FREECAD ASSEMBLY — COMPONENT RECIPES ("InterconnectIO_Box_full_511-1000")

This assembly document has 5 components, labeled P0..P4 below (a component is one placed body or linked part). 2 of them carry a construction recipe — the FreeCAD feature program that regenerates the part from scratch, quoted from this document or its linked companion documents; the rest are supplied as boundary geometry only. No exploded tour is included for this assembly.
COMPONENT P0 — recipe-attached ("rail_left", modeled in this document).
Construction recipe (the document's own serialized feature program — sketch geometry with constraints, then the solid features built on it; lengths are millimeters unless a unit is written):

FEATURE [PartDesign::Body] Body  label="slot"
  Origin = -> Origin119
  Placement = pos=(0,6.008,0) rot=(0,0,1;0rad)
FEATURE [Sketcher::SketchObject] Sketch
  FullyConstrained = true
  MapMode = 5
  Support = -> [XY_Plane120]
  sketch-geometry (4):
    g0: LineSegment StartX=-2.36 StartY=2.5 StartZ=0 EndX=2.36 EndY=2.5 EndZ=0
    g1: LineSegment StartX=2.36 StartY=2.5 StartZ=0 EndX=2.36 EndY=156 EndZ=0
    g2: LineSegment StartX=2.36 StartY=156 StartZ=0 EndX=-2.36 EndY=156 EndZ=0
    g3: LineSegment StartX=-2.36 StartY=156 StartZ=0 EndX=-2.36 EndY=2.5 EndZ=0
  constraints (12):
    c: Coincident(g0,g1)
    c: Coincident(g1,g2)
    c: Coincident(g2,g3)
    c: Coincident(g3,g0)
    c: Horizontal(g0)
    c: Horizontal(g2)
    c: Vertical(g1)
    c: Vertical(g3)
    c: DistanceX(g2,g2) = 4.72
    c: DistanceY(g0,g-1) = -2.5
    c: DistanceX(g0,g-1) = 2.36
    c: DistanceY(g1,g1) = 153.5
FEATURE [Sketcher::SketchObject] Sketch003
  FullyConstrained = true
  MapMode = 5
  Support = -> [XY_Plane120]
  sketch-geometry (8):
    g0: LineSegment StartX=-1 StartY=0 StartZ=0 EndX=-1 EndY=153 EndZ=0
    g1: ArcOfCircle CenterX=-7.01053 CenterY=152.083 CenterZ=0 NormalX=0 NormalY=0 NormalZ=1 AngleXU=0 Radius=6.08 StartAngle=0.151318 EndAngle=0.699927
    g2: LineSegment StartX=-2.36 StartY=156 StartZ=0 EndX=-2.86 EndY=156 EndZ=0
    g3: ArcOfCircle CenterX=-3459.01 CenterY=157.297 CenterZ=0 NormalX=0 NormalY=0 NormalZ=1 AngleXU=0 Radius=3456.16 StartAngle=6.24055 EndAngle=6.28281
    g4: LineSegment StartX=-4 StartY=0 StartZ=0 EndX=-4 EndY=2.5 EndZ=0
    g5: LineSegment StartX=-4 StartY=2.5 StartZ=0 EndX=-6 EndY=2.5 EndZ=0
    g6: LineSegment StartX=-4 StartY=0 StartZ=0 EndX=-1 EndY=0 EndZ=0
    g7: LineSegment StartX=-6 StartY=10 StartZ=0 EndX=-6 EndY=2.5 EndZ=0
  constraints (27):
    c: Vertical(g0)
    c: Coincident(g1,g0)
    c: Coincident(g2,g1)
    c: Horizontal(g2)
    c: Coincident(g3,g2)
    c: DistanceX(g2,g2) = 0.5
    c: Diameter(g3) = 6912.31
    c: PointOnObject(g6,g-1)
    c: Vertical(g4)
    c: Coincident(g5,g4)
    c: Horizontal(g5)
    c: Coincident(g6,g4)
    c: Coincident(g7,g3)
    c: Coincident(g7,g5)
    c: DistanceX(g6,g6) = 3
    c: Vertical(g7)
    c: DistanceX(g5,g5) = 2
    c: DistanceY(g7,g7) = 7.5
    c: DistanceY(g4,g4) = 2.5
    c: DistanceY(g4,g-1) = 0
    c: DistanceY(g3,g2) = 146
    c: DistanceY(g0,g0) = 153
    c: DistanceX(g0,g-1) = 1
    c: DistanceX(g6,g-1) = 1
    c: DistanceY(g6,g0) = 0
    c: Radius(g1) = 6.08
    c: DistanceX(g1,g0) = 1.36
FEATURE [PartDesign::Pad] Pad
  Direction = (0,0,1)
  Length = 8
  Length2 = 10
  Profile = -> Sketch003
  ReferenceAxis = -> Sketch003 [N_Axis]
  Type = 0
FEATURE [PartDesign::Pad] Pad001
  BaseFeature = -> Pad
  Direction = (0,0,1)
  Length = 5
  Length2 = 10
  Profile = -> Sketch
  ReferenceAxis = -> Sketch [N_Axis]
  Type = 0
FEATURE [Sketcher::SketchObject] Sketch011
  FullyConstrained = true
  MapMode = 5
  Support = -> [XY_Plane120]
  sketch-geometry (6):
    g0: LineSegment StartX=1 StartY=0 StartZ=0 EndX=10 EndY=0 EndZ=0
    g1: LineSegment StartX=4.36 StartY=156 StartZ=0 EndX=2.36 EndY=156 EndZ=0
    g2: LineSegment StartX=1 StartY=153 StartZ=0 EndX=1 EndY=0 EndZ=0
    g3: ArcOfCircle CenterX=7.01053 CenterY=152.083 CenterZ=0 NormalX=0 NormalY=0 NormalZ=1 AngleXU=0 Radius=6.08 StartAngle=2.44167 EndAngle=2.99027
    g4: LineSegment StartX=10 StartY=0 StartZ=0 EndX=10 EndY=10.5 EndZ=0
    g5: ArcOfCircle CenterX=-6386.74 CenterY=-164.597 CenterZ=0 NormalX=0 NormalY=0 NormalZ=1 AngleXU=0 Radius=6399.14 StartAngle=0.027366 EndAngle=0.050121
  constraints (20):
    c: Coincident(g2,g0)
    c: Horizontal(g0)
    c: Horizontal(g1)
    c: Vertical(g2)
    c: PointOnObject(g0,g-1)
    c: Coincident(g1,g3)
    c: Coincident(g2,g3)
    c: DistanceX(g2,g1) = 1.36
    c: DistanceY(g2,g1) = 3
    c: DistanceX(g1,g1) = 2
    c: DistanceX(g-1,g0) = 1
    c: DistanceY(g2,g2) = 153
    c: Radius(g3) = 6.08
    c: Coincident(g4,g0)
    c: DistanceY(g4,g4) = 10.5
    c: Coincident(g5,g4)
    c: Coincident(g5,g1)
    c: Radius(g5) = 6399.14
    c: DistanceX(g0,g0) = 9
    c: DistanceX(g-1,g4) = 10
FEATURE [PartDesign::Pad] Pad003
  BaseFeature = -> Pad001
  Direction = (0,0,1)
  Length = 8
  Length2 = 10
  Profile = -> Sketch011
  ReferenceAxis = -> Sketch011 [N_Axis]
  Type = 0
FEATURE [PartDesign::Body] Body003  label="rail"
  Group = -> [Sketch003,Pad,Sketch,Pad001,Sketch011,Pad003]
  Origin = -> Origin120
  Tip = -> Pad003
FEATURE [Sketcher::SketchObject] Sketch013
  FullyConstrained = false
  MapMode = 5
  Placement = pos=(0,0,0) rot=(0.57735,0.57735,0.57735;2.0944rad)
  Support = -> [YZ_Plane121]
  sketch-geometry (5):
    g0: LineSegment StartX=6.01175 StartY=0 StartZ=0 EndX=36.0118 EndY=0 EndZ=0
    g1: LineSegment StartX=36.0118 StartY=0 StartZ=0 EndX=36.0118 EndY=-2 EndZ=0
    g2: LineSegment StartX=8.01175 StartY=-30 StartZ=0 EndX=6.01175 EndY=-30 EndZ=0
    g3: LineSegment StartX=6.01175 StartY=-30 StartZ=0 EndX=6.01175 EndY=0 EndZ=0
    g4: ArcOfCircle CenterX=42.4201 CenterY=-36.4083 CenterZ=0 NormalX=0 NormalY=0 NormalZ=1 AngleXU=0 Radius=35 StartAngle=1.75493 EndAngle=2.95746
  constraints (14):
    c: Coincident(g0,g1)
    c: Coincident(g2,g3)
    c: Coincident(g3,g0)
    c: Horizontal(g0)
    c: Horizontal(g2)
    c: Vertical(g1)
    c: Vertical(g3)
    c: PointOnObject(g0,g-1)
    c: DistanceX(g0,g0) = 30
    c: Coincident(g1,g4)
    c: Coincident(g2,g4)
    c: DistanceY(g1,g1) = 2
    c: DistanceX(g2,g2) = 2
    c: Radius(g4) = 35
FEATURE [PartDesign::Pad] Pad005
  Direction = (1,-2e-16,3e-16)
  Length = 6
  Length2 = 10
  Placement = pos=(0,0,0) rot=(0.57735,0.57735,0.57735;2.0944rad)
  Profile = -> Sketch013
  ReferenceAxis = -> Sketch013 [N_Axis]
  Type = 0
FEATURE [PartDesign::Fillet] Fillet
  Base = -> Pad005 [Edge5]
  BaseFeature = -> Pad005
  Placement = pos=(0,0,0) rot=(0.57735,0.57735,0.57735;2.0944rad)
  Radius = 2
  SupportTransform = false
  UseAllEdges = false
FEATURE [PartDesign::Fillet] Fillet001
  Base = -> Fillet [Edge17]
  BaseFeature = -> Fillet
  Placement = pos=(0,0,0) rot=(0.57735,0.57735,0.57735;2.0944rad)
  Radius = 2
  SupportTransform = false
  UseAllEdges = false
FEATURE [PartDesign::Body] Body004  label="sideforce"
  Group = -> [Sketch013,Pad005,Fillet,Fillet001]
  Origin = -> Origin121
  Placement = pos=(-4.016,0.057,0) rot=(0,0,1;0rad)
  Tip = -> Fillet001
FEATURE [Sketcher::SketchObject] Sketch019
  FullyConstrained = false
  MapMode = 5
  Placement = pos=(0,0,0) rot=(-0.57735,0.57735,0.57735;4.18879rad)
  Support = -> [YZ_Plane122]
  sketch-geometry (10):
    g0: LineSegment StartX=-156.003 StartY=8.00103 StartZ=0 EndX=-137.423 EndY=8.00103 EndZ=0
    g1: LineSegment StartX=-137.423 StartY=8.00103 StartZ=0 EndX=-137.423 EndY=8.88796 EndZ=0
    g2: LineSegment StartX=-139.803 StartY=35.8702 StartZ=0 EndX=-153.603 EndY=35.8702 EndZ=0
    g3: ArcOfCircle CenterX=-136.888 CenterY=21.0784 CenterZ=0 NormalX=0 NormalY=0 NormalZ=1 AngleXU=0 Radius=11.34 StartAngle=1.74764 EndAngle=4.59202
    g4: ArcOfCircle CenterX=-153.603 CenterY=33.4702 CenterZ=0 NormalX=0 NormalY=0 NormalZ=1 AngleXU=0 Radius=2.4 StartAngle=1.5708 EndAngle=3.27078
    g5: ArcOfCircle CenterX=-139.803 CenterY=33.4702 CenterZ=0 NormalX=0 NormalY=0 NormalZ=1 AngleXU=0 Radius=2.4 StartAngle=0.566257 EndAngle=1.5708
    g6: ArcOfCircle CenterX=-230.704 CenterY=20.6405 CenterZ=0 NormalX=0 NormalY=0 NormalZ=1 AngleXU=0 Radius=75.763 StartAngle=6.11557 EndAngle=6.44921
    g7: Circle CenterX=-150.473 CenterY=13.3301 CenterZ=0 NormalX=0 NormalY=0 NormalZ=1 AngleXU=0 Radius=3
    g8: ArcOfCircle CenterX=-138.362 CenterY=8.88796 CenterZ=0 NormalX=0 NormalY=0 NormalZ=1 AngleXU=0 Radius=0.939281 StartAngle=0 EndAngle=1.45042
    g9: ArcOfCircle CenterX=-139.174 CenterY=33.8702 CenterZ=0 NormalX=0 NormalY=0 NormalZ=1 AngleXU=0 Radius=1.65446 StartAngle=4.88923 EndAngle=6.84944
  constraints (20):
    c: Coincident(g0,g1)
    c: Horizontal(g0)
    c: Horizontal(g2)
    c: Vertical(g1)
    c: Tangent(g2,g4) = -1.5708
    c: Tangent(g2,g5) = -1.5708
    c: Radius(g4) = 2.4
    c: Radius(g5) = 2.4
    c: DistanceX(g2,g2) = 13.8
    c: DistanceY(g0,g4) = 25.16
    c: DistanceX(g4,g2) = 2.38
    c: Radius(g3) = 11.34
    c: Coincident(g6,g0)
    c: Coincident(g6,g4)
    c: DistanceX(g0,g0) = 18.58
    c: Diameter(g7) = 6
    c: Tangent(g3,g8) = 1.5708
    c: Tangent(g1,g8) = -1.5708
    c: Tangent(g3,g9) = 1.5708
    c: Tangent(g5,g9) = -1.5708
FEATURE [PartDesign::Pad] Pad006
  Direction = (-1,2e-16,-3e-16)
  Length = 7
  Length2 = 10
  Placement = pos=(0,0,0) rot=(0.57735,0.57735,0.57735;2.0944rad)
  Profile = -> Sketch019
  ReferenceAxis = -> Sketch019 [N_Axis]
  Type = 0
FEATURE [PartDesign::Body] Body007  label="finger"
  Group = -> [Sketch019,Pad006]
  Origin = -> Origin122
  Placement = pos=(-2.654,-0.011,8.013) rot=(0,1,0;3.14159rad)
  Tip = -> Pad006
FEATURE [Sketcher::SketchObject] Sketch020
  FullyConstrained = true
  MapMode = 5
  Placement = pos=(0,0,0) rot=(1,0,0;1.5708rad)
  Support = -> [XZ_Plane124]
  sketch-geometry (4):
    g0: ArcOfCircle CenterX=5.9 CenterY=35 CenterZ=0 NormalX=0 NormalY=0 NormalZ=1 AngleXU=0 Radius=3 StartAngle=4e-16 EndAngle=3.14159
    g1: ArcOfCircle CenterX=5.9 CenterY=13 CenterZ=0 NormalX=0 NormalY=0 NormalZ=1 AngleXU=0 Radius=3 StartAngle=3.14159 EndAngle=6.28319
    g2: LineSegment StartX=2.9 StartY=35 StartZ=0 EndX=2.9 EndY=13 EndZ=0
    g3: LineSegment StartX=8.9 StartY=13 StartZ=0 EndX=8.9 EndY=35 EndZ=0
  constraints (10):
    c: Tangent(g0,g2) = -1.5708
    c: Tangent(g2,g1) = -1.5708
    c: Tangent(g1,g3) = -1.5708
    c: Tangent(g3,g0) = -1.5708
    c: Equal(g0,g1)
    c: Vertical(g2)
    c: DistanceY(g1,g0) = 22
    c: DistanceX(g1,g1) = 6
    c: DistanceY(g-1,g1) = 13
    c: DistanceX(g-1,g1) = 5.9
FEATURE [PartDesign::Pad] Pad007
  Direction = (0,-1,-2e-16)
  Length = 2
  Length2 = 10
  Placement = pos=(0,0,0) rot=(1,0,0;1.5708rad)
  Profile = -> Sketch020
  ReferenceAxis = -> Sketch020 [N_Axis]
  Type = 0
FEATURE [PartDesign::Body] Body009  label="slotscrew"
  Group = -> [Sketch020,Pad007]
  Origin = -> Origin123
  Placement = pos=(-0.028,0.002,-39.747) rot=(0,0,1;0rad)
  Tip = -> Pad007
COMPONENT P1 — recipe-attached ("rail_right", modeled in this document).
Construction recipe (the document's own serialized feature program — sketch geometry with constraints, then the solid features built on it; lengths are millimeters unless a unit is written):

FEATURE [Sketcher::SketchObject] Sketch021
  AttachmentOffset = pos=(0,0,3) rot=(0,0,1;0rad)
  FullyConstrained = true
  MapMode = 5
  Placement = pos=(0,0,3) rot=(0,0,1;0rad)
  Support = -> [XY_Plane125]
  sketch-geometry (4):
    g0: LineSegment StartX=-2.36 StartY=2.5 StartZ=0 EndX=2.36 EndY=2.5 EndZ=0
    g1: LineSegment StartX=2.36 StartY=2.5 StartZ=0 EndX=2.36 EndY=156 EndZ=0
    g2: LineSegment StartX=2.36 StartY=156 StartZ=0 EndX=-2.36 EndY=156 EndZ=0
    g3: LineSegment StartX=-2.36 StartY=156 StartZ=0 EndX=-2.36 EndY=2.5 EndZ=0
  constraints (12):
    c: Coincident(g0,g1)
    c: Coincident(g1,g2)
    c: Coincident(g2,g3)
    c: Coincident(g3,g0)
    c: Horizontal(g0)
    c: Horizontal(g2)
    c: Vertical(g1)
    c: Vertical(g3)
    c: DistanceX(g2,g2) = 4.72
    c: DistanceY(g0,g-1) = -2.5
    c: DistanceX(g0,g-1) = 2.36
    c: DistanceY(g1,g1) = 153.5
FEATURE [Sketcher::SketchObject] Sketch022
  FullyConstrained = true
  MapMode = 5
  Support = -> [XY_Plane125]
  sketch-geometry (8):
    g0: LineSegment StartX=-1 StartY=0 StartZ=0 EndX=-1 EndY=153 EndZ=0
    g1: ArcOfCircle CenterX=-7.01053 CenterY=152.083 CenterZ=0 NormalX=0 NormalY=0 NormalZ=1 AngleXU=0 Radius=6.08 StartAngle=0.151318 EndAngle=0.699927
    g2: LineSegment StartX=-2.36 StartY=156 StartZ=0 EndX=-2.86 EndY=156 EndZ=0
    g3: ArcOfCircle CenterX=-3459.01 CenterY=157.297 CenterZ=0 NormalX=0 NormalY=0 NormalZ=1 AngleXU=0 Radius=3456.16 StartAngle=6.24055 EndAngle=6.28281
    g4: LineSegment StartX=-4 StartY=0 StartZ=0 EndX=-4 EndY=2.5 EndZ=0
    g5: LineSegment StartX=-4 StartY=2.5 StartZ=0 EndX=-6 EndY=2.5 EndZ=0
    g6: LineSegment StartX=-4 StartY=0 StartZ=0 EndX=-1 EndY=0 EndZ=0
    g7: LineSegment StartX=-6 StartY=10 StartZ=0 EndX=-6 EndY=2.5 EndZ=0
  constraints (27):
    c: Vertical(g0)
    c: Coincident(g1,g0)
    c: Coincident(g2,g1)
    c: Horizontal(g2)
    c: Coincident(g3,g2)
    c: DistanceX(g2,g2) = 0.5
    c: Diameter(g3) = 6912.31
    c: PointOnObject(g6,g-1)
    c: Vertical(g4)
    c: Coincident(g5,g4)
    c: Horizontal(g5)
    c: Coincident(g6,g4)
    c: Coincident(g7,g3)
    c: Coincident(g7,g5)
    c: DistanceX(g6,g6) = 3
    c: Vertical(g7)
    c: DistanceX(g5,g5) = 2
    c: DistanceY(g7,g7) = 7.5
    c: DistanceY(g4,g4) = 2.5
    c: DistanceY(g4,g-1) = 0
    c: DistanceY(g3,g2) = 146
    c: DistanceY(g0,g0) = 153
    c: DistanceX(g0,g-1) = 1
    c: DistanceX(g6,g-1) = 1
    c: DistanceY(g6,g0) = 0
    c: Radius(g1) = 6.08
    c: DistanceX(g1,g0) = 1.36
FEATURE [PartDesign::Pad] Pad008
  Direction = (0,0,1)
  Length = 8
  Length2 = 10
  Profile = -> Sketch022
  ReferenceAxis = -> Sketch022 [N_Axis]
  Type = 0
FEATURE [PartDesign::Pad] Pad009
  BaseFeature = -> Pad008
  Direction = (0,0,1)
  Length = 5
  Length2 = 10
  Profile = -> Sketch021
  ReferenceAxis = -> Sketch021 [N_Axis]
  Type = 0
FEATURE [Sketcher::SketchObject] Sketch023
  FullyConstrained = true
  MapMode = 5
  Support = -> [XY_Plane125]
  sketch-geometry (6):
    g0: LineSegment StartX=1 StartY=0 StartZ=0 EndX=10 EndY=0 EndZ=0
    g1: LineSegment StartX=4.36 StartY=156 StartZ=0 EndX=2.36 EndY=156 EndZ=0
    g2: LineSegment StartX=1 StartY=153 StartZ=0 EndX=1 EndY=0 EndZ=0
    g3: ArcOfCircle CenterX=7.01053 CenterY=152.083 CenterZ=0 NormalX=0 NormalY=0 NormalZ=1 AngleXU=0 Radius=6.08 StartAngle=2.44167 EndAngle=2.99027
    g4: LineSegment StartX=10 StartY=0 StartZ=0 EndX=10 EndY=10.5 EndZ=0
    g5: ArcOfCircle CenterX=-6386.74 CenterY=-164.597 CenterZ=0 NormalX=0 NormalY=0 NormalZ=1 AngleXU=0 Radius=6399.14 StartAngle=0.027366 EndAngle=0.050121
  constraints (20):
    c: Coincident(g2,g0)
    c: Horizontal(g0)
    c: Horizontal(g1)
    c: Vertical(g2)
    c: PointOnObject(g0,g-1)
    c: Coincident(g1,g3)
    c: Coincident(g2,g3)
    c: DistanceX(g2,g1) = 1.36
    c: DistanceY(g2,g1) = 3
    c: DistanceX(g1,g1) = 2
    c: DistanceX(g-1,g0) = 1
    c: DistanceY(g2,g2) = 153
    c: Radius(g3) = 6.08
    c: Coincident(g4,g0)
    c: DistanceY(g4,g4) = 10.5
    c: Coincident(g5,g4)
    c: Coincident(g5,g1)
    c: Radius(g5) = 6399.14
    c: DistanceX(g0,g0) = 9
    c: DistanceX(g-1,g4) = 10
FEATURE [PartDesign::Pad] Pad010
  BaseFeature = -> Pad009
  Direction = (0,0,1)
  Length = 8
  Length2 = 10
  Profile = -> Sketch023
  ReferenceAxis = -> Sketch023 [N_Axis]
  Type = 0
FEATURE [PartDesign::Body] Body010  label="rail001"
  Group = -> [Sketch022,Pad008,Sketch021,Pad009,Sketch023,Pad010]
  Origin = -> Origin125
  Tip = -> Pad010
FEATURE [Sketcher::SketchObject] Sketch025
  FullyConstrained = false
  MapMode = 5
  Placement = pos=(0,0,0) rot=(0.57735,0.57735,0.57735;2.0944rad)
  Support = -> [YZ_Plane126]
  sketch-geometry (5):
    g0: LineSegment StartX=6.01175 StartY=0 StartZ=0 EndX=36.0118 EndY=0 EndZ=0
    g1: LineSegment StartX=36.0118 StartY=0 StartZ=0 EndX=36.0118 EndY=-2 EndZ=0
    g2: LineSegment StartX=8.01175 StartY=-30 StartZ=0 EndX=6.01175 EndY=-30 EndZ=0
    g3: LineSegment StartX=6.01175 StartY=-30 StartZ=0 EndX=6.01175 EndY=0 EndZ=0
    g4: ArcOfCircle CenterX=42.4201 CenterY=-36.4083 CenterZ=0 NormalX=0 NormalY=0 NormalZ=1 AngleXU=0 Radius=35 StartAngle=1.75493 EndAngle=2.95746
  constraints (14):
    c: Coincident(g0,g1)
    c: Coincident(g2,g3)
    c: Coincident(g3,g0)
    c: Horizontal(g0)
    c: Horizontal(g2)
    c: Vertical(g1)
    c: Vertical(g3)
    c: PointOnObject(g0,g-1)
    c: DistanceX(g0,g0) = 30
    c: Coincident(g1,g4)
    c: Coincident(g2,g4)
    c: DistanceY(g1,g1) = 2
    c: DistanceX(g2,g2) = 2
    c: Radius(g4) = 35
FEATURE [PartDesign::Pad] Pad012
  Direction = (1,-2e-16,3e-16)
  Length = 6
  Length2 = 10
  Placement = pos=(0,0,0) rot=(0.57735,0.57735,0.57735;2.0944rad)
  Profile = -> Sketch025
  ReferenceAxis = -> Sketch025 [N_Axis]
  Type = 0
FEATURE [PartDesign::Fillet] Fillet002
  Base = -> Pad012 [Edge5]
  BaseFeature = -> Pad012
  Placement = pos=(0,0,0) rot=(0.57735,0.57735,0.57735;2.0944rad)
  Radius = 2
  SupportTransform = false
  UseAllEdges = false
FEATURE [PartDesign::Fillet] Fillet003
  Base = -> Fillet002 [Edge17]
  BaseFeature = -> Fillet002
  Placement = pos=(0,0,0) rot=(0.57735,0.57735,0.57735;2.0944rad)
  Radius = 2
  SupportTransform = false
  UseAllEdges = false
FEATURE [PartDesign::Body] Body011  label="sideforce001"
  Group = -> [Sketch025,Pad012,Fillet002,Fillet003]
  Origin = -> Origin126
  Placement = pos=(2,0,8) rot=(0,1,0;3.14159rad)
  Tip = -> Fillet003
FEATURE [Sketcher::SketchObject] Sketch026
  FullyConstrained = false
  MapMode = 5
  Placement = pos=(0,0,0) rot=(-0.57735,0.57735,0.57735;4.18879rad)
  Support = -> [YZ_Plane127]
  sketch-geometry (10):
    g0: LineSegment StartX=-156.003 StartY=8.00103 StartZ=0 EndX=-137.423 EndY=8.00103 EndZ=0
    g1: LineSegment StartX=-137.423 StartY=8.00103 StartZ=0 EndX=-137.423 EndY=8.88796 EndZ=0
    g2: LineSegment StartX=-139.803 StartY=35.8702 StartZ=0 EndX=-153.603 EndY=35.8702 EndZ=0
    g3: ArcOfCircle CenterX=-136.888 CenterY=21.0784 CenterZ=0 NormalX=0 NormalY=0 NormalZ=1 AngleXU=0 Radius=11.34 StartAngle=1.74764 EndAngle=4.59202
    g4: ArcOfCircle CenterX=-153.603 CenterY=33.4702 CenterZ=0 NormalX=0 NormalY=0 NormalZ=1 AngleXU=0 Radius=2.4 StartAngle=1.5708 EndAngle=3.27078
    g5: ArcOfCircle CenterX=-139.803 CenterY=33.4702 CenterZ=0 NormalX=0 NormalY=0 NormalZ=1 AngleXU=0 Radius=2.4 StartAngle=0.566257 EndAngle=1.5708
    g6: ArcOfCircle CenterX=-230.704 CenterY=20.6405 CenterZ=0 NormalX=0 NormalY=0 NormalZ=1 AngleXU=0 Radius=75.763 StartAngle=6.11557 EndAngle=6.44921
    g7: Circle CenterX=-150.473 CenterY=13.3301 CenterZ=0 NormalX=0 NormalY=0 NormalZ=1 AngleXU=0 Radius=3
    g8: ArcOfCircle CenterX=-138.362 CenterY=8.88796 CenterZ=0 NormalX=0 NormalY=0 NormalZ=1 AngleXU=0 Radius=0.939281 StartAngle=0 EndAngle=1.45042
    g9: ArcOfCircle CenterX=-139.174 CenterY=33.8702 CenterZ=0 NormalX=0 NormalY=0 NormalZ=1 AngleXU=0 Radius=1.65446 StartAngle=4.88923 EndAngle=6.84944
  constraints (20):
    c: Coincident(g0,g1)
    c: Horizontal(g0)
    c: Horizontal(g2)
    c: Vertical(g1)
    c: Tangent(g2,g4) = -1.5708
    c: Tangent(g2,g5) = -1.5708
    c: Radius(g4) = 2.4
    c: Radius(g5) = 2.4
    c: DistanceX(g2,g2) = 13.8
    c: DistanceY(g0,g4) = 25.16
    c: DistanceX(g4,g2) = 2.38
    c: Radius(g3) = 11.34
    c: Coincident(g6,g0)
    c: Coincident(g6,g4)
    c: DistanceX(g0,g0) = 18.58
    c: Diameter(g7) = 6
    c: Tangent(g3,g8) = 1.5708
    c: Tangent(g1,g8) = -1.5708
    c: Tangent(g3,g9) = 1.5708
    c: Tangent(g5,g9) = -1.5708
FEATURE [PartDesign::Pad] Pad013
  Direction = (-1,2e-16,-3e-16)
  Length = 7
  Length2 = 10
  Placement = pos=(0,0,0) rot=(0.57735,0.57735,0.57735;2.0944rad)
  Profile = -> Sketch026
  ReferenceAxis = -> Sketch026 [N_Axis]
  Type = 0
FEATURE [PartDesign::Body] Body012  label="finger001"
  Group = -> [Sketch026,Pad013]
  Origin = -> Origin127
  Placement = pos=(4.278,-0.01,-0.012) rot=(0,0,1;0rad)
  Tip = -> Pad013
FEATURE [Sketcher::SketchObject] Sketch027
  FullyConstrained = true
  MapMode = 5
  Placement = pos=(0,0,0) rot=(1,0,0;1.5708rad)
  Support = -> [XZ_Plane129]
  sketch-geometry (4):
    g0: ArcOfCircle CenterX=5.9 CenterY=35 CenterZ=0 NormalX=0 NormalY=0 NormalZ=1 AngleXU=0 Radius=3 StartAngle=4e-16 EndAngle=3.14159
    g1: ArcOfCircle CenterX=5.9 CenterY=13 CenterZ=0 NormalX=0 NormalY=0 NormalZ=1 AngleXU=0 Radius=3 StartAngle=3.14159 EndAngle=6.28319
    g2: LineSegment StartX=2.9 StartY=35 StartZ=0 EndX=2.9 EndY=13 EndZ=0
    g3: LineSegment StartX=8.9 StartY=13 StartZ=0 EndX=8.9 EndY=35 EndZ=0
  constraints (10):
    c: Tangent(g0,g2) = -1.5708
    c: Tangent(g2,g1) = -1.5708
    c: Tangent(g1,g3) = -1.5708
    c: Tangent(g3,g0) = -1.5708
    c: Equal(g0,g1)
    c: Vertical(g2)
    c: DistanceY(g1,g0) = 22
    c: DistanceX(g1,g1) = 6
    c: DistanceY(g-1,g1) = 13
    c: DistanceX(g-1,g1) = 5.9
FEATURE [PartDesign::Pad] Pad014
  Direction = (0,-1,-2e-16)
  Length = 2
  Length2 = 10
  Placement = pos=(0,0,0) rot=(1,0,0;1.5708rad)
  Profile = -> Sketch027
  ReferenceAxis = -> Sketch027 [N_Axis]
  Type = 0
FEATURE [PartDesign::Body] Body013  label="slotscrew001"
  Group = -> [Sketch027,Pad014]
  Origin = -> Origin128
  Placement = pos=(-0.013,-4.05,-39.977) rot=(0,0,1;0rad)
  Tip = -> Pad014
COMPONENT P2 — geometry summary ("selftest_bd"; no construction recipe available for this part):
  bounding box: 300.0 x 157.6 x 21.9 mm
  tessellated surface: 562,012 triangles
  volume: 107416 mm^3 (10% of its bounding box)
COMPONENT P3 — geometry summary ("InterconnectIO"; no construction recipe available for this part):
  bounding box: 406.4 x 221.1 x 22.9 mm
  tessellated surface: 1,395,088 triangles
  volume: 244619 mm^3 (12% of its bounding box)
COMPONENT P4 — geometry summary ("PRM-14460 (DESKTOP)"; no construction recipe available for this part):
  bounding box: 437.1 x 203.2 x 43.7 mm
  tessellated surface: 55,688 triangles
  volume: 630323 mm^3 (16% of its bounding box)
  symmetry: 2-fold rotationally symmetric about the x axis; 2-fold rotationally symmetric about the y axis; 2-fold rotationally symmetric about the z axis; mirror-symmetric across its x mid-plane, y mid-plane, z mid-plane
PROVENANCE & LICENSES
A FreeCAD (.FCStd) document from a public repository crawl; recipes are the document's own serialized feature recipes (and, for linked parts, companion documents' recipes).
License: cern-ohl.
